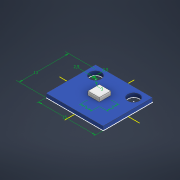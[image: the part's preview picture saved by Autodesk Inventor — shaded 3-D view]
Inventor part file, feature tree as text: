
AUTODESK INVENTOR PART (.ipt)
format: ipt  version: 2021 (Build 250183000, 183)  size: 126,464 bytes
history: native  units: mm
features: extrude x2, other x1, sketch x1
ambient origin geometry x8: Origin, YZ Plane, XZ Plane, XY Plane, X Axis, Y Axis, Z Axis, Center Point
bodies: Body1 (feature_tree)
feature tree (4):
  other  "Drucksensor"
  sketch  "Skizze1"  dims[d0=15.0mm d1=13.0mm d10=3.0mm d11=3.0mm d12=3.0mm d13=2.5mm d14=2.5mm d15=1.0mm d16=0.0mm d17=2.0mm d18=0.0mm]
  extrude  "Extrusion3"  Depth=13.0mm
  extrude  "Extrusion4"  Depth=3.0mm
